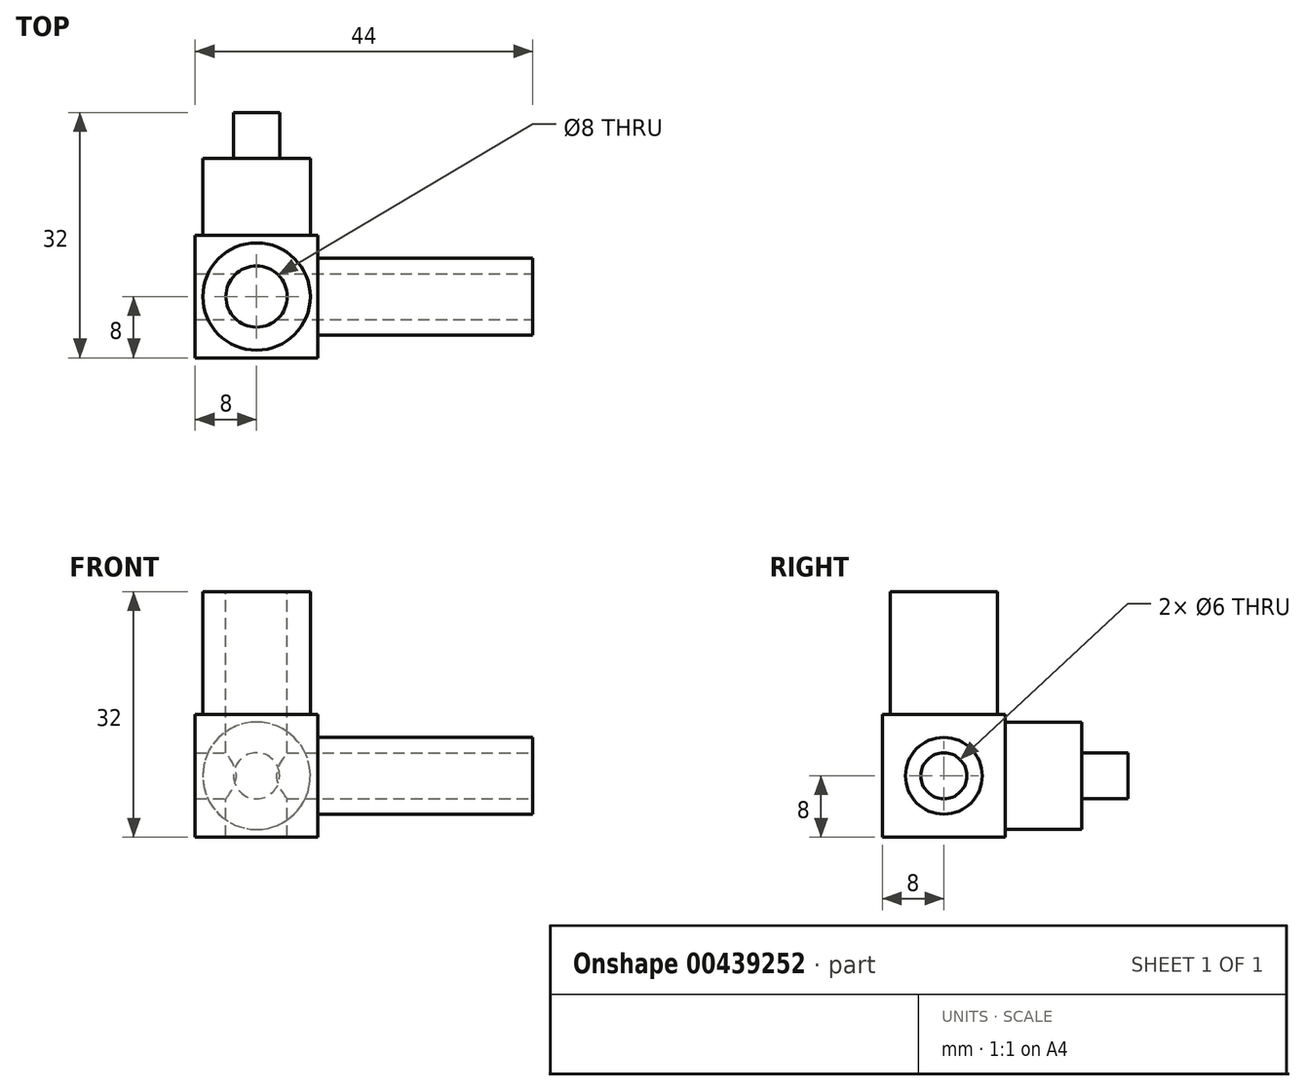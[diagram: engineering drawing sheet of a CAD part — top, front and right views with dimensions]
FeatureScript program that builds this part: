
annotation { "Feature Type Name" : "Feature", "Feature Type Description" : "" }
export const myFeature = defineFeature(function(context is Context, id is Id, definition is map)
    precondition{}
    {
        {
            var Q0;
            Q0=qCreatedBy(makeId("Top.planeOp"),FACE);
            var sketch = newSketch(context, id + "F0", { "sketchPlane" : qUnion([Q0])});
            skLineSegment(sketch, "E0.bottom", {"start": v(8, -8) * mm, "end": v(-8, -8) * mm});
            skLineSegment(sketch, "E0.top", {"start": v(8, 8) * mm, "end": v(-8, 8) * mm});
            skLineSegment(sketch, "E0.left", {"start": v(8, -8) * mm, "end": v(8, 8) * mm});
            skLineSegment(sketch, "E0.right", {"start": v(-8, -8) * mm, "end": v(-8, 8) * mm});
            skPoint(sketch, "E0.middle", {"position": v(0, 0) * mm});
            skSolve(sketch);
        }
        {
            var Q0;
            Q0=makeQuery(id+"F0.imprint","IMPRINT",FACE,{"disambiguationData":[TD([[makeQuery(id+"F0.imprint","IMPRINT",EDGE,{"derivedFrom":sQuery(id+"F0.wireOp",EDGE,"E0.bottom")}),-1.0]])]});
            extrude(context, id + "F1", {"entities" : qUnion([Q0]), "depth" : 16 * mm});
        }
        {
            var Q0;
            Q0=makeQuery(id+"F1.opExtrude","SWEPT_FACE",FACE,{"disambiguationData":[OSD([sQuery(id+"F0.wireOp",EDGE,"E0.left")])]});
            var sketch = newSketch(context, id + "F2", { "sketchPlane" : qUnion([Q0])});
            skLineSegment(sketch, "E1", {"start": v(0, 0) * mm, "end": v(0, 16) * mm, "construction": true});
            skLineSegment(sketch, "E2", {"start": v(-8, 8) * mm, "end": v(8, 8) * mm, "construction": true});
            skCircle(sketch, "E3", {"center": v(0, 8) * mm, "radius": 3 * mm});
            skCircle(sketch, "E4", {"center": v(0, 8) * mm, "radius": 5 * mm});
            skSolve(sketch);
        }
        {
            var Q0;
            Q0=makeQuery(id+"F2.imprint","IMPRINT",FACE,{"disambiguationData":[TD([[makeQuery(id+"F2.imprint","IMPRINT",EDGE,{"derivedFrom":sQuery(id+"F2.wireOp",EDGE,"E3")}),1.0]])]});
            extrude(context, id + "F3", {"entities" : qUnion([Q0]), "operationType" : NewBodyOperationType.REMOVE, "oppositeDirection" : true, "depth" : 25 * mm});
        }
        {
            var Q0;
            Q0=makeQuery(id+"F2.imprint","IMPRINT",FACE,{"disambiguationData":[TD([[makeQuery(id+"F2.imprint","IMPRINT",EDGE,{"derivedFrom":sQuery(id+"F2.wireOp",EDGE,"E3")}),-1.0]])]});
            extrude(context, id + "F4", {"entities" : qUnion([Q0]), "operationType" : NewBodyOperationType.ADD, "depth" : 28 * mm});
        }
        {
            var Q0;
            Q0=makeQuery(id+"F1.opExtrude","CAP_FACE",FACE,{"disambiguationData":[OSD([sQuery(id+"F0.wireOp",EDGE,"E0.bottom"),sQuery(id+"F0.wireOp",EDGE,"E0.top"),sQuery(id+"F0.wireOp",EDGE,"E0.left"),sQuery(id+"F0.wireOp",EDGE,"E0.right")])],"isStart":false});
            var sketch = newSketch(context, id + "F5", { "sketchPlane" : qUnion([Q0])});
            skCircle(sketch, "E5", {"center": v(0, 0) * mm, "radius": 4 * mm});
            skCircle(sketch, "E6", {"center": v(0, 0) * mm, "radius": 7 * mm});
            skSolve(sketch);
        }
        {
            var Q0;
            Q0=makeQuery(id+"F5.imprint","IMPRINT",FACE,{"disambiguationData":[TD([[makeQuery(id+"F5.imprint","IMPRINT",EDGE,{"derivedFrom":sQuery(id+"F5.wireOp",EDGE,"E5")}),1.0]])]});
            extrude(context, id + "F6", {"entities" : qUnion([Q0]), "operationType" : NewBodyOperationType.REMOVE, "oppositeDirection" : true, "depth" : 25 * mm});
        }
        {
            var Q0;
            Q0=makeQuery(id+"F5.imprint","IMPRINT",FACE,{"disambiguationData":[TD([[makeQuery(id+"F5.imprint","IMPRINT",EDGE,{"derivedFrom":sQuery(id+"F5.wireOp",EDGE,"E5")}),-1.0]])]});
            extrude(context, id + "F7", {"entities" : qUnion([Q0]), "operationType" : NewBodyOperationType.ADD, "depth" : 16 * mm});
        }
        {
            var Q0;
            Q0=makeQuery(id+"F1.opExtrude","SWEPT_FACE",FACE,{"disambiguationData":[OSD([sQuery(id+"F0.wireOp",EDGE,"E0.top")])]});
            var sketch = newSketch(context, id + "F8", { "sketchPlane" : qUnion([Q0])});
            skLineSegment(sketch, "E7", {"start": v(-8, 8) * mm, "end": v(8.7, 8) * mm, "construction": true});
            skPoint(sketch, "E7.endSnap0", {"position": v(8, 8) * mm});
            skLineSegment(sketch, "E8", {"start": v(0, 16) * mm, "end": v(0, 0) * mm, "construction": true});
            skCircle(sketch, "E9", {"center": v(0, 8) * mm, "radius": 7 * mm});
            skCircle(sketch, "E10", {"center": v(0, 8) * mm, "radius": 3 * mm});
            skSolve(sketch);
        }
        {
            var Q0;
            Q0=makeQuery(id+"F8.imprint","IMPRINT",FACE,{"disambiguationData":[TD([[makeQuery(id+"F8.imprint","IMPRINT",EDGE,{"derivedFrom":sQuery(id+"F8.wireOp",EDGE,"E10")}),1.0]])]});
            extrude(context, id + "F9", {"entities" : qUnion([Q0]), "operationType" : NewBodyOperationType.ADD, "depth" : 16 * mm});
        }
        {
            var Q0;
            Q0=makeQuery(id+"F8.imprint","IMPRINT",FACE,{"disambiguationData":[TD([[makeQuery(id+"F8.imprint","IMPRINT",EDGE,{"derivedFrom":sQuery(id+"F8.wireOp",EDGE,"E9")}),1.0]])]});
            extrude(context, id + "F10", {"entities" : qUnion([Q0]), "operationType" : NewBodyOperationType.ADD, "depth" : 10 * mm});
        }
    });
